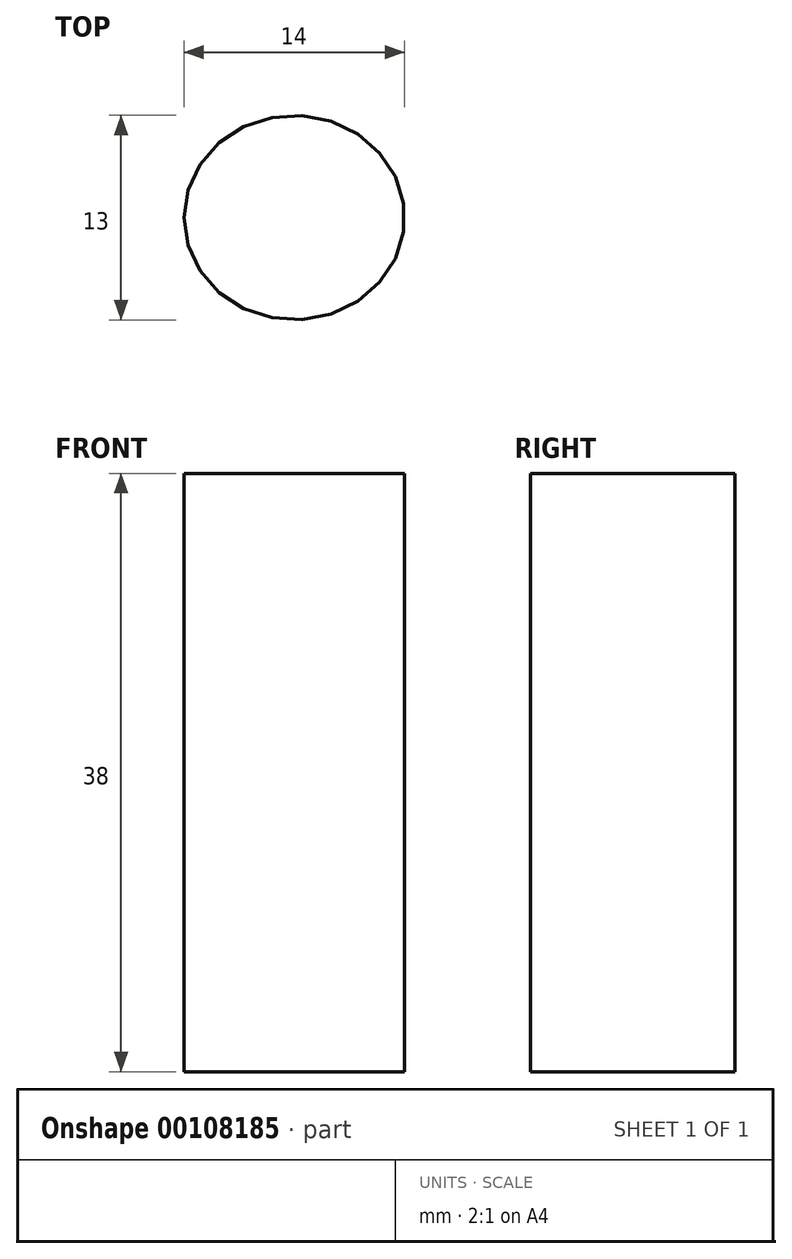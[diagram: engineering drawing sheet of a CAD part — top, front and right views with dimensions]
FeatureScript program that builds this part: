
annotation { "Feature Type Name" : "Feature", "Feature Type Description" : "" }
export const myFeature = defineFeature(function(context is Context, id is Id, definition is map)
    precondition{}
    {
        {
            var Q0;
            Q0=qCreatedBy(makeId("Top.planeOp"),FACE);
            var sketch = newSketch(context, id + "F0", { "sketchPlane" : qUnion([Q0])});
            skCircle(sketch, "E0", {"center": v(0, 0) * mm, "radius": 6.5 * mm});
            skEllipse(sketch, "E1", {"center": v(0, 0) * mm, "majorRadius": 7 * mm, "minorRadius": 6.5 * mm, "majorAxis": v(-1, 0)});
            skSolve(sketch);
        }
        {
            var Q0;
            Q0=makeQuery(id+"F0.imprint","IMPRINT",FACE,{"disambiguationData":[TD([[makeQuery(id+"F0.imprint","IMPRINT",EDGE,{"derivedFrom":sQuery(id+"F0.wireOp",EDGE,"E0")}),1.0]])]});
            var Q1;
            {var subQ0=sQuery(id+"F0.wireOp",EDGE,"E1");var subQ1=sQuery(id+"F0.wireOp",EDGE,"E0");var subQ2=makeQuery(id+"F0.imprint","INTERSECT",VERTEX,{"disambiguationData":[OD(0.0)],"derivedFrom":[subQ1,subQ0]});Q1=makeQuery(id+"F0.imprint","IMPRINT",FACE,{"disambiguationData":[TD([[makeQuery(id+"F0.imprint","IMPRINT",EDGE,{"disambiguationData":[TD([[subQ2,-1.0]])],"derivedFrom":subQ1}),-1.0]])]});}
            var Q2;
            {var subQ0=sQuery(id+"F0.wireOp",EDGE,"E1");var subQ1=sQuery(id+"F0.wireOp",EDGE,"E0");var subQ2=makeQuery(id+"F0.imprint","INTERSECT",VERTEX,{"disambiguationData":[OD(0.0)],"derivedFrom":[subQ1,subQ0]});Q2=makeQuery(id+"F0.imprint","IMPRINT",FACE,{"disambiguationData":[TD([[makeQuery(id+"F0.imprint","IMPRINT",EDGE,{"disambiguationData":[TD([[subQ2,1.0]])],"derivedFrom":subQ1}),-1.0]])]});}
            extrude(context, id + "F1", {"entities" : qUnion([Q0, Q1, Q2]), "depth" : 38 * mm});
        }
    });
